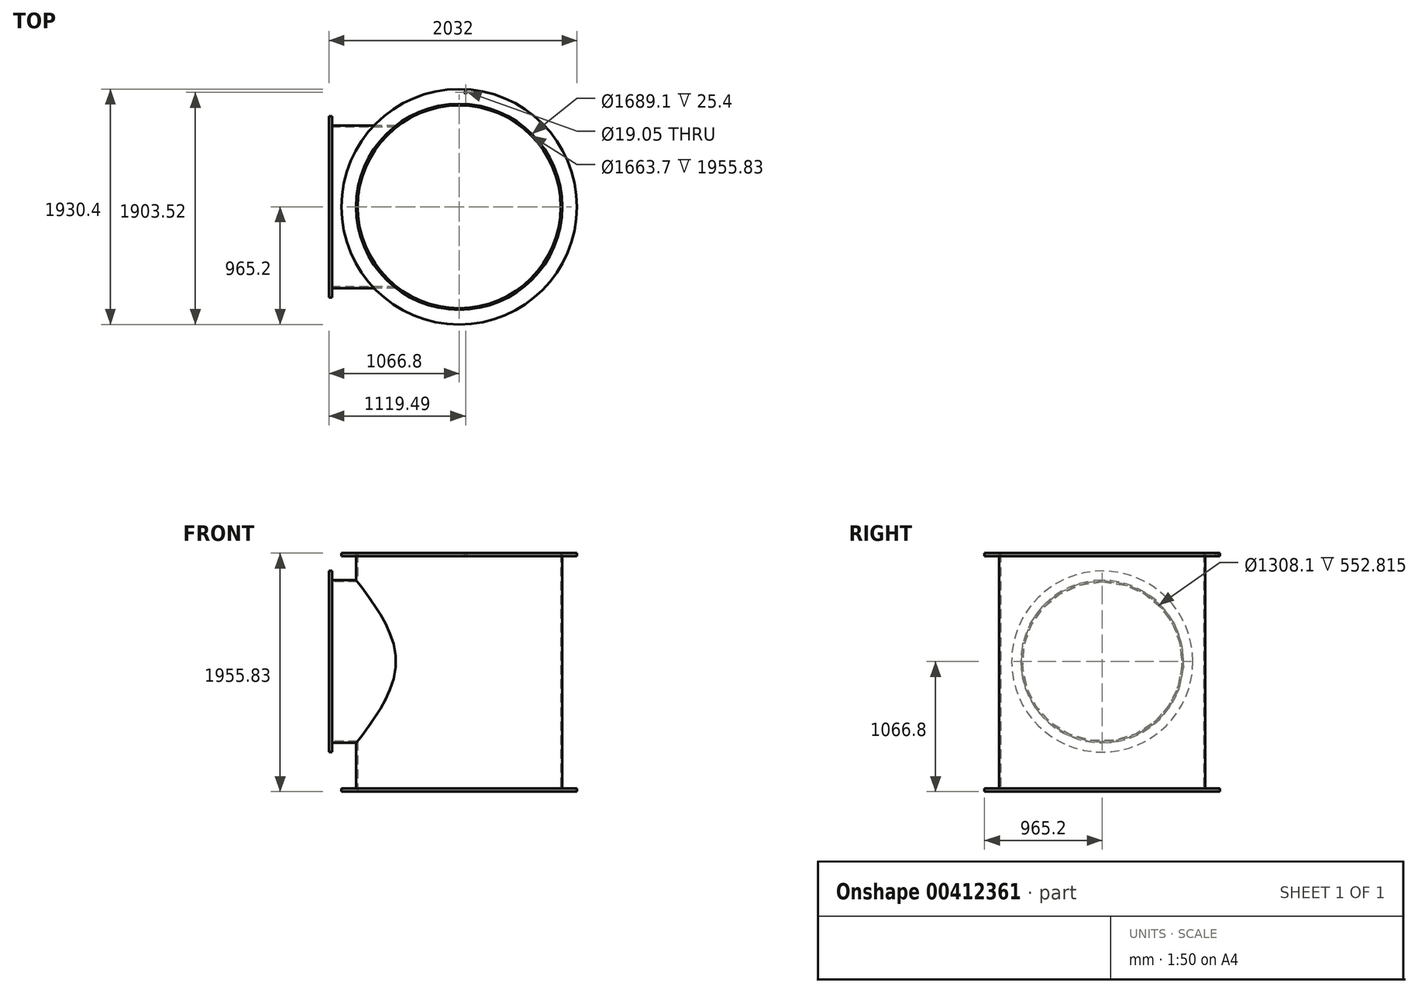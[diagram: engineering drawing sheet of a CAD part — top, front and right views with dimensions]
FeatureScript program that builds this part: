
annotation { "Feature Type Name" : "Feature", "Feature Type Description" : "" }
export const myFeature = defineFeature(function(context is Context, id is Id, definition is map)
    precondition{}
    {
        {
            var Q0;
            Q0=qCreatedBy(makeId("Top.planeOp"),FACE);
            var sketch = newSketch(context, id + "F0", { "sketchPlane" : qUnion([Q0])});
            skCircle(sketch, "E0", {"center": v(0, 0) * mm, "radius": 965.2 * mm});
            skCircle(sketch, "E1", {"center": v(0, 0) * mm, "radius": 844.55 * mm});
            skCircle(sketch, "E2", {"center": v(0, 0) * mm, "radius": 831.85 * mm});
            skSolve(sketch);
        }
        {
            var Q0;
            Q0 = qSketchRegion(id + "F0", true);
            extrude(context, id + "F1", {"entities" : qUnion([Q0]), "depth" : 25.4 * mm});
        }
        {
            var Q0;
            Q0=makeQuery(id+"F0.imprint","IMPRINT",FACE,{"disambiguationData":[TD([[makeQuery(id+"F0.imprint","IMPRINT",EDGE,{"derivedFrom":sQuery(id+"F0.wireOp",EDGE,"E1")}),1.0]])]});
            extrude(context, id + "F2", {"entities" : qUnion([Q0]), "operationType" : NewBodyOperationType.ADD, "depth" : 1828.8 * mm + 127 * mm + 7 / 203.2 * mm});
        }
        {
            var Q0;
            Q0=makeQuery(id+"F2.opExtrude","CAP_FACE",FACE,{"disambiguationData":[OSD([sQuery(id+"F0.wireOp",EDGE,"E1"),sQuery(id+"F0.wireOp",EDGE,"E2")])],"isStart":false});
            var sketch = newSketch(context, id + "F3", { "sketchPlane" : qUnion([Q0])});
            skCircle(sketch, "E3", {"center": v(0, 0) * mm, "radius": 965.2 * mm});
            skCircle(sketch, "E4", {"center": v(0, 0) * mm, "radius": 844.55 * mm});
            skCircle(sketch, "E5", {"center": v(0, 0) * mm, "radius": 939.8 * mm, "construction": true});
            skLineSegment(sketch, "E6", {"start": v(0, 0) * mm, "end": v(0, 1081.52) * mm, "construction": true});
            skLineSegment(sketch, "E7", {"start": v(0, 0) * mm, "end": v(60.76, 1081.92) * mm, "construction": true});
            skPoint(sketch, "E8", {"position": v(52.7, 938.32) * mm});
            skSolve(sketch);
        }
        {
            var Q0;
            Q0=makeQuery(id+"F3.imprint","IMPRINT",FACE,{"disambiguationData":[TD([[makeQuery(id+"F3.imprint","IMPRINT",EDGE,{"derivedFrom":sQuery(id+"F3.wireOp",EDGE,"E3")}),1.0]])]});
            extrude(context, id + "F4", {"entities" : qUnion([Q0]), "oppositeDirection" : true, "depth" : 25.4 * mm});
        }
        {
            var Q0;
            Q0=sQuery(id+"F3.wireOp",VERTEX,"E8");
            var Q1;
            Q1=makeQuery(id+"F4.opExtrude","SWEPT_BODY",BODY,{"disambiguationData":[OSD([sQuery(id+"F3.wireOp",EDGE,"E3"),sQuery(id+"F3.wireOp",EDGE,"E4")])]});
            hole(context, id + "F5", {"style" : HoleStyle.SIMPLE, "endStyle" : HoleEndStyle.THROUGH, "holeDiameter" : 19.05 * mm, "isTappedThrough" : true, "tappedDepth" : 12.7 * mm, "tapClearance" : 3, "startFromSketch" : true, "locations" : qUnion([Q0]), "scope" : qUnion([Q1])});
        }
        {
            var Q0;
            Q0=qCreatedBy(makeId("Right.planeOp"),FACE);
            cPlane(context, id + "F6", {"entities" : qUnion([Q0]), "cplaneType" : CPlaneType.OFFSET, "offset" : 1066.8 * mm, "oppositeDirection" : true, "width" : 152.4 * mm, "height" : 152.4 * mm});
        }
        {
            var Q0;
            Q0=qCreatedBy(id+"F6.planeOp",FACE);
            var sketch = newSketch(context, id + "F7", { "sketchPlane" : qUnion([Q0])});
            skLineSegment(sketch, "E9", {"start": v(0, 0) * mm, "end": v(0, 1066.8) * mm, "construction": true});
            skCircle(sketch, "E10", {"center": v(0, 1066.8) * mm, "radius": 742.95 * mm});
            skCircle(sketch, "E11", {"center": v(0, 1066.8) * mm, "radius": 717.55 * mm, "construction": true});
            skCircle(sketch, "E12", {"center": v(0, 1066.8) * mm, "radius": 666.75 * mm});
            skCircle(sketch, "E13", {"center": v(0, 1066.8) * mm, "radius": 654.05 * mm});
            skSolve(sketch);
        }
        {
            var Q0;
            Q0=makeQuery(id+"F7.imprint","IMPRINT",FACE,{"disambiguationData":[TD([[makeQuery(id+"F7.imprint","IMPRINT",EDGE,{"derivedFrom":sQuery(id+"F7.wireOp",EDGE,"E10")}),1.0]])]});
            extrude(context, id + "F8", {"entities" : qUnion([Q0]), "depth" : 25.4 * mm});
        }
        {
            var Q0;
            Q0=makeQuery(id+"F7.imprint","IMPRINT",FACE,{"disambiguationData":[TD([[makeQuery(id+"F7.imprint","IMPRINT",EDGE,{"derivedFrom":sQuery(id+"F7.wireOp",EDGE,"E12")}),1.0]])]});
            var Q1;
            Q1=makeQuery(id+"F1.opExtrude","SWEPT_BODY",BODY,{"disambiguationData":[OSD([sQuery(id+"F0.wireOp",EDGE,"E0"),sQuery(id+"F0.wireOp",EDGE,"E1")])]});
            extrude(context, id + "F9", {"entities" : qUnion([Q0]), "operationType" : NewBodyOperationType.ADD, "endBound" : BoundingType.UP_TO_BODY, "endBoundEntityBody" : qUnion([Q1]), "depth" : 640.08 * mm});
        }
        {
            var Q0;
            Q0=makeQuery(id+"F7.imprint","IMPRINT",FACE,{"disambiguationData":[TD([[makeQuery(id+"F7.imprint","IMPRINT",EDGE,{"derivedFrom":sQuery(id+"F7.wireOp",EDGE,"E13")}),1.0]])]});
            extrude(context, id + "F10", {"entities" : qUnion([Q0]), "operationType" : NewBodyOperationType.REMOVE, "depth" : 784.86 * mm});
        }
    });
